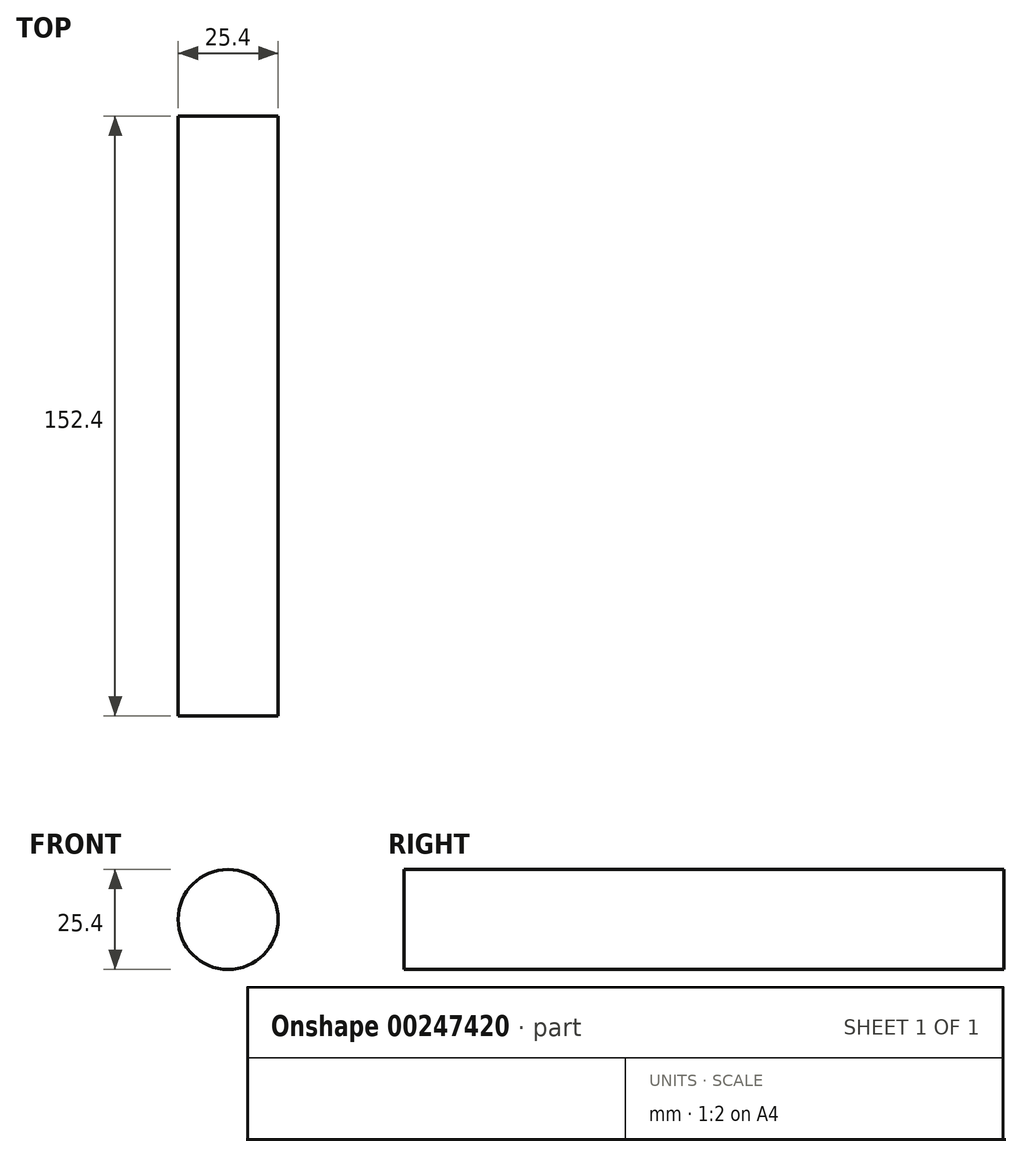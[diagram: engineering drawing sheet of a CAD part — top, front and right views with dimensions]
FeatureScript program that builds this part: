
annotation { "Feature Type Name" : "Feature", "Feature Type Description" : "" }
export const myFeature = defineFeature(function(context is Context, id is Id, definition is map)
    precondition{}
    {
        {
            var Q0;
            Q0=qCreatedBy(makeId("Front.planeOp"),FACE);
            var sketch = newSketch(context, id + "F0", { "sketchPlane" : qUnion([Q0])});
            skCircle(sketch, "E0", {"center": v(0, 0) * mm, "radius": 12.7 * mm});
            skSolve(sketch);
        }
        {
            var Q0;
            Q0 = qSketchRegion(id + "F0", true);
            extrude(context, id + "F1", {"entities" : qUnion([Q0]), "depth" : 152.4 * mm});
        }
    });
